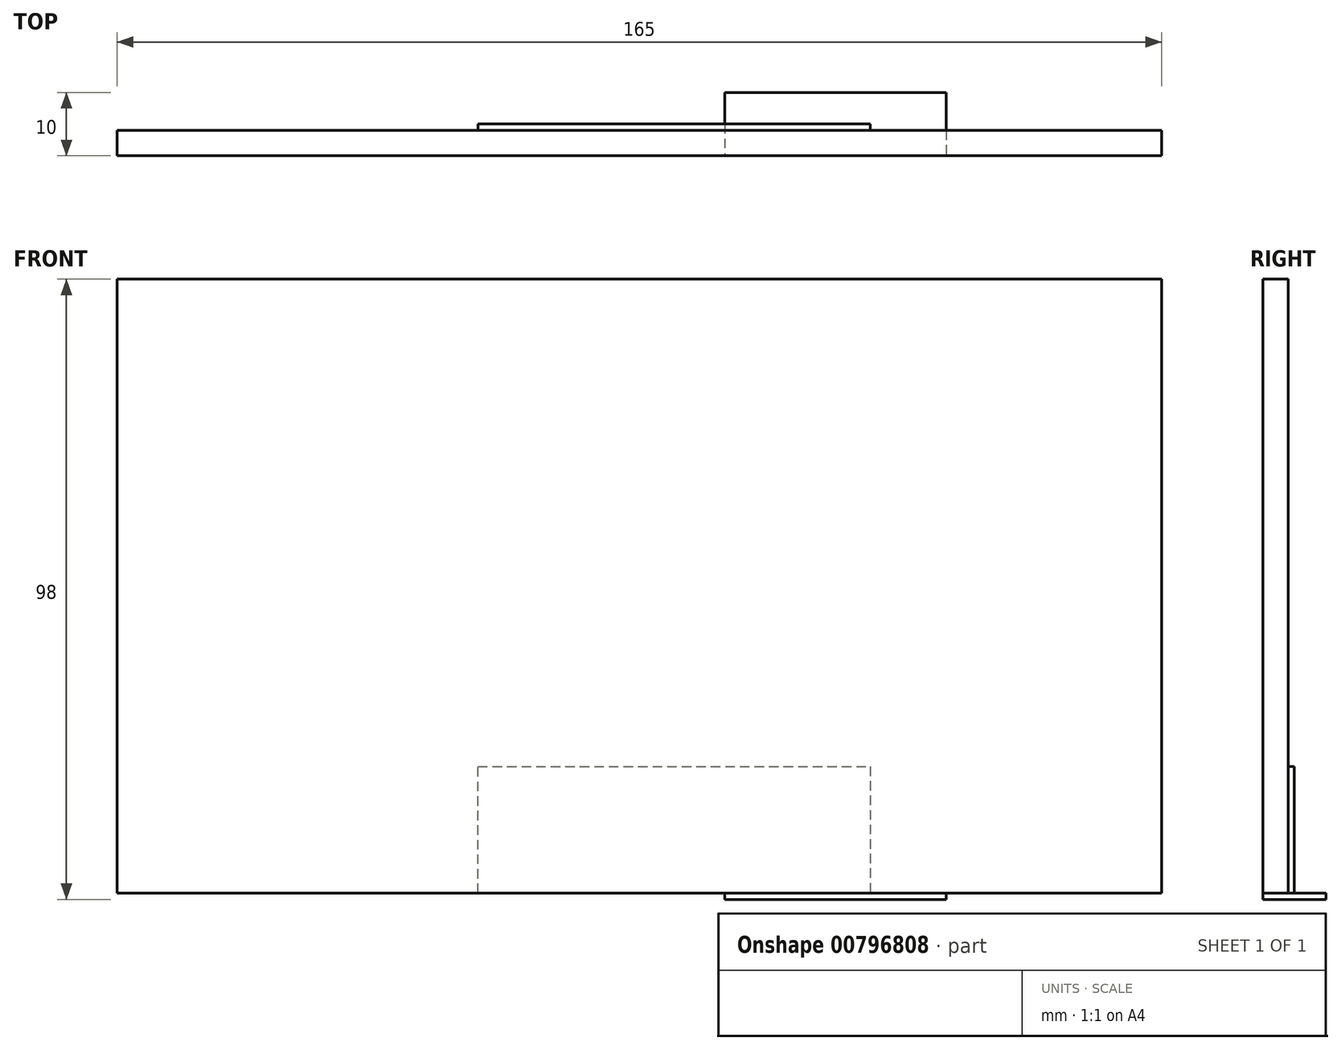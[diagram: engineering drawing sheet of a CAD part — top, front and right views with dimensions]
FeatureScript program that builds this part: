
annotation { "Feature Type Name" : "Feature", "Feature Type Description" : "" }
export const myFeature = defineFeature(function(context is Context, id is Id, definition is map)
    precondition{}
    {
        {
            var Q0;
            Q0=qCreatedBy(makeId("Front.planeOp"),FACE);
            var sketch = newSketch(context, id + "F0", { "sketchPlane" : qUnion([Q0])});
            skLineSegment(sketch, "E0.bottom", {"start": v(-82.5, 48.5) * mm, "end": v(82.5, 48.5) * mm});
            skLineSegment(sketch, "E0.top", {"start": v(-82.5, -48.5) * mm, "end": v(13.5, -48.5) * mm});
            skLineSegment(sketch, "E0.left", {"start": v(-82.5, 48.5) * mm, "end": v(-82.5, -48.5) * mm});
            skLineSegment(sketch, "E0.right", {"start": v(82.5, 48.5) * mm, "end": v(82.5, -48.5) * mm});
            skPoint(sketch, "E0.middle", {"position": v(0, 0) * mm});
            skLineSegment(sketch, "E1", {"start": v(-25.5, -48.5) * mm, "end": v(-25.5, -28.5) * mm});
            skLineSegment(sketch, "E2", {"start": v(-25.5, -28.5) * mm, "end": v(36.5, -28.5) * mm});
            skLineSegment(sketch, "E3", {"start": v(36.5, -28.5) * mm, "end": v(36.5, -48.5) * mm});
            skLineSegment(sketch, "E4.trimOffspring", {"start": v(48.5, -48.5) * mm, "end": v(82.5, -48.5) * mm});
            skLineSegment(sketch, "E5", {"start": v(13.5, -48.5) * mm, "end": v(13.5, -49.5) * mm});
            skLineSegment(sketch, "E6", {"start": v(13.5, -49.5) * mm, "end": v(48.5, -49.5) * mm});
            skLineSegment(sketch, "E7", {"start": v(48.5, -49.5) * mm, "end": v(48.5, -48.5) * mm});
            skLineSegment(sketch, "E8", {"start": v(13.5, -48.5) * mm, "end": v(48.5, -48.5) * mm});
            skSolve(sketch);
        }
        {
            var Q0;
            Q0=makeQuery(id+"F0.imprint","IMPRINT",FACE,{"disambiguationData":[TD([[makeQuery(id+"F0.imprint","IMPRINT",EDGE,{"derivedFrom":sQuery(id+"F0.wireOp",EDGE,"E0.bottom")}),-1.0]])]});
            extrude(context, id + "F1", {"entities" : qUnion([Q0]), "oppositeDirection" : true, "depth" : 4 * mm, "offsetDistance" : 25 * mm});
        }
        {
            var Q0;
            {var subQ0=sQuery(id+"F0.wireOp",EDGE,"E1");Q0=makeQuery(id+"F0.imprint","IMPRINT",FACE,{"disambiguationData":[TD([[makeQuery(id+"F0.imprint","IMPRINT",EDGE,{"derivedFrom":subQ0}),-1.0]])]});}
            extrude(context, id + "F2", {"entities" : qUnion([Q0]), "operationType" : NewBodyOperationType.ADD, "oppositeDirection" : true, "depth" : 5 * mm, "offsetDistance" : 25 * mm});
        }
        {
            var Q0;
            {var subQ1=sQuery(id+"F0.wireOp",EDGE,"E5");Q0=makeQuery(id+"F0.imprint","IMPRINT",FACE,{"disambiguationData":[TD([[makeQuery(id+"F0.imprint","IMPRINT",EDGE,{"derivedFrom":subQ1}),1.0]])]});}
            extrude(context, id + "F3", {"entities" : qUnion([Q0]), "oppositeDirection" : true, "depth" : 10 * mm, "offsetDistance" : 25 * mm});
        }
    });
